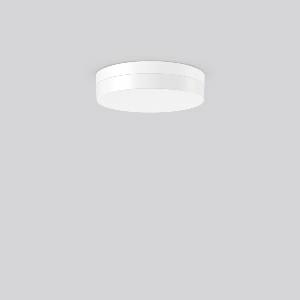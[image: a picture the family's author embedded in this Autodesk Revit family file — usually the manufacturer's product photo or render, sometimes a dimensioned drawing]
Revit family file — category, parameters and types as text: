
# Revit family: flat_slim_round_312629_002_19_94aa
name_source: partatom
category: Lighting Fixtures
units: mm (PartAtom-declared; Revit-internal decimal feet)

## family parameters
Cut with Voids When Loaded = No
Host = Face
Light Source = No
Part Type = Normal
Room Calculation Point = No
Round Connector Dimension = Use Diameter
Shared = No

## types (1)
- MultiLumen 1 830 (1 x LED Modul 830, 1250 lm, 3000)
    Apparent Load = 13 VA
    CIE Flux Codes = 38 68 89 82 100
    Color Rendering = 80
    Color Temperature = 3000
    Default Elevation = 1800 mm
    Height = 75 mm
    Lamp = 1 x LED Modul 830
    Lamp Light Flux = 1250 lm
    Lamp count = 1
    Length = 300 mm
    Lifetime = 50000 h
    Luminous efficacy = 96 lm/W
    Manufacturer = RZB
    ModVariant = No
    Model = 312629.002.19
    Mounting Place = Ceiling
    Mounting Type = Surface mounted
    Number of Poles = 1
    OnlyDefault = Yes
    Power Factor = 1
    Product Name = FLAT SLIM round
    Product group = Surface mounted ceiling and wall luminaires
    ProductGroupID = 305
    Protection Class = Protection class I
    Protection Degree = Degree of protection
    RLX_Detail_Level = 1
    RLX_Emergency_Light_Flux = 0 lm
    RLX_Emergency_Type = 0
    RLX_Emergency_Type_DB = No
    RlxData = <blob elided: 16953 chars, md5=c946d50d>
    Socket = socket
    Standby Power = 0 W
    System Light Flux = 1250 lm
    System Power = 13 W
    Type Comments = MultiLumen 1 830
    Type Image = 312629.002.jpg
    URL = http://relux.com
    VarID = multilumen_1_830
    Voltage = 0 V
    Weight = 0.00 kg
    Width = 0 mm  [stored 0 ft]

note: [stored X ft] marks values corroborated as IEEE doubles in the binary element streams (Revit-internal decimal feet)

## geometry (parser evidence)
native form markers: Blend x4, Sweep x12
no freeform markers — native parametric forms only
